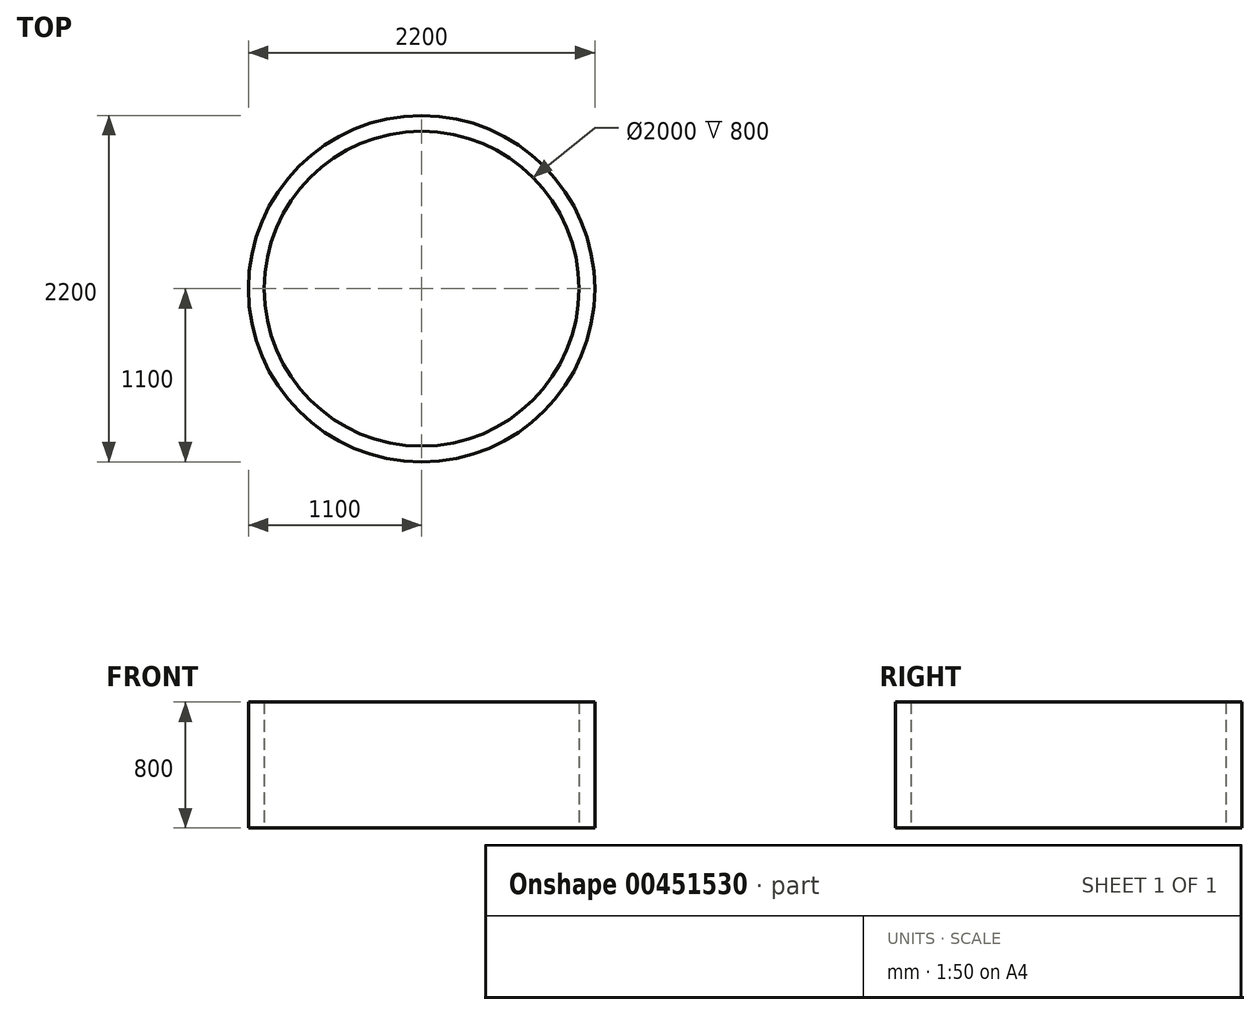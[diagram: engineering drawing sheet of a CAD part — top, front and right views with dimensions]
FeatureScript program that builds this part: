
annotation { "Feature Type Name" : "Feature", "Feature Type Description" : "" }
export const myFeature = defineFeature(function(context is Context, id is Id, definition is map)
    precondition{}
    {
        {
            var Q0;
            Q0=qCreatedBy(makeId("Top.planeOp"),FACE);
            var sketch = newSketch(context, id + "F0", { "sketchPlane" : qUnion([Q0])});
            skCircle(sketch, "E0", {"center": v(0, 0) * mm, "radius": 1100 * mm});
            skCircle(sketch, "E1", {"center": v(0, 0) * mm, "radius": 1000 * mm});
            skSolve(sketch);
        }
        {
            var Q0;
            Q0 = qSketchRegion(id + "F0", true);
            extrude(context, id + "F1", {"entities" : qUnion([Q0]), "depth" : 800 * mm});
        }
    });
